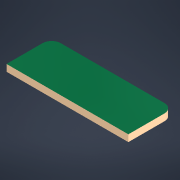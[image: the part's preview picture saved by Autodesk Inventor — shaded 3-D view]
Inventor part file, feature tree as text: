
AUTODESK INVENTOR PART (.ipt)
format: ipt  version: 2021 (Build 250183000, 183)  size: 104,960 bytes
history: native  units: mm
features: extrude x1, sketch x1
ambient origin geometry x8: Origin, YZ Plane, XZ Plane, XY Plane, X Axis, Y Axis, Z Axis, Center Point
bodies: Solid1 (feature_tree)
feature tree (2):
  extrude  "Extrusion1"  Depth=10.0mm
  sketch  "Sketch1"  dims[d0=27.0mm d1=10.0mm d2=2.0mm d3=1.5mm d4=0.0mm]
